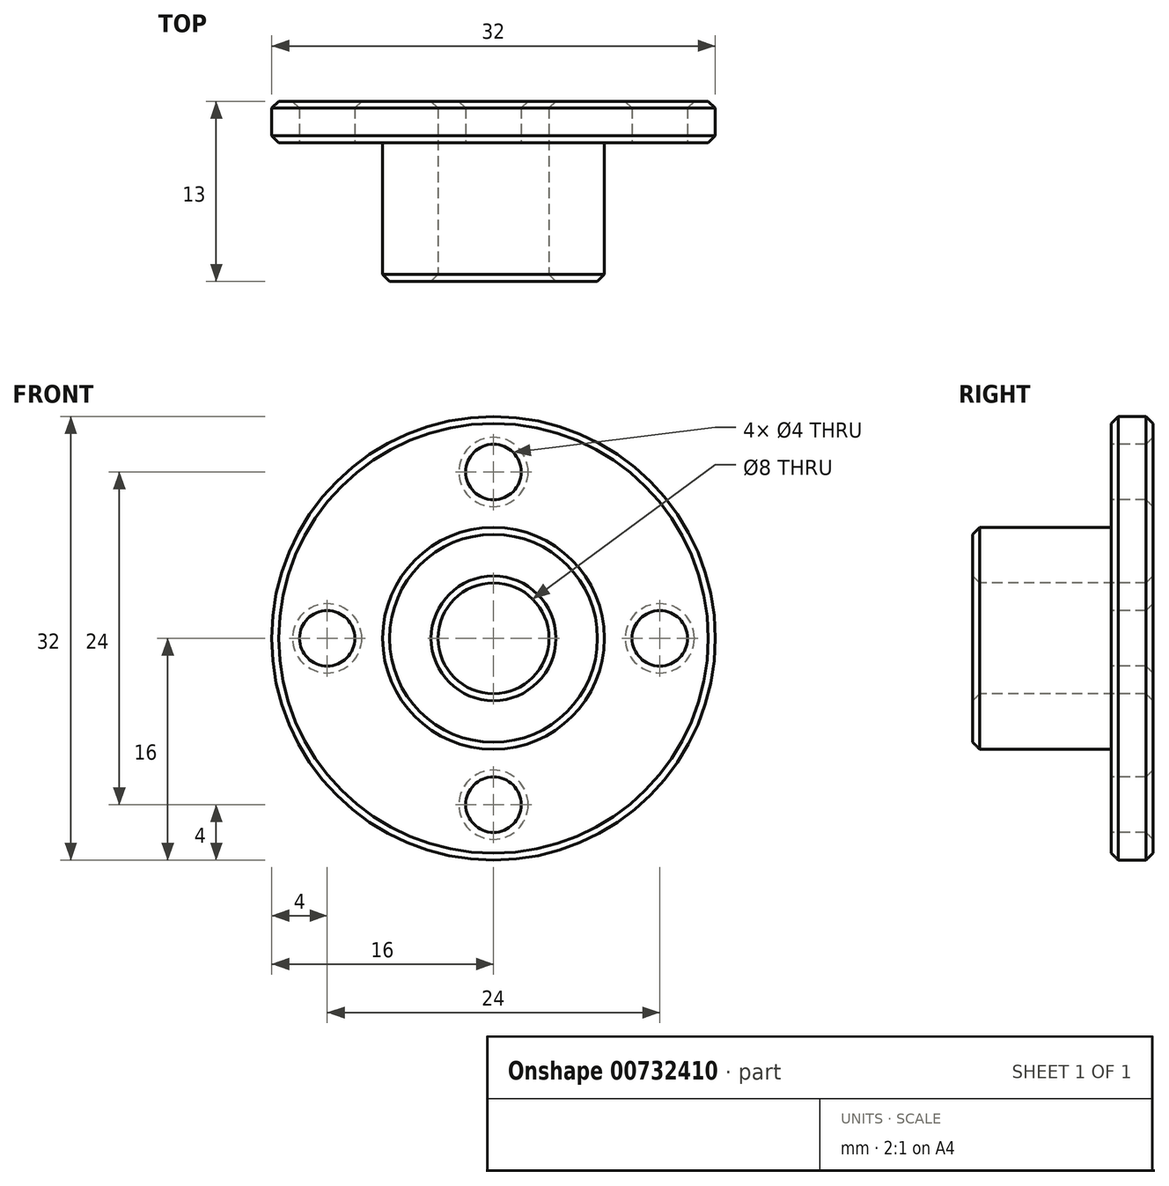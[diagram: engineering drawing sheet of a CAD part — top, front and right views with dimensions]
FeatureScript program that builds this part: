
annotation { "Feature Type Name" : "Feature", "Feature Type Description" : "" }
export const myFeature = defineFeature(function(context is Context, id is Id, definition is map)
    precondition{}
    {
        {
            var Q0;
            Q0=qCreatedBy(makeId("Front.planeOp"),FACE);
            var sketch = newSketch(context, id + "F0", { "sketchPlane" : qUnion([Q0])});
            skCircle(sketch, "E0", {"center": v(0, 0) * mm, "radius": 16 * mm});
            skSolve(sketch);
        }
        {
            var Q0;
            Q0 = qSketchRegion(id + "F0", true);
            extrude(context, id + "F1", {"entities" : qUnion([Q0]), "depth" : 3 * mm, "offsetDistance" : 25 * mm});
        }
        {
            var Q0;
            Q0=makeQuery(id+"F1.opExtrude","CAP_FACE",FACE,{"disambiguationData":[OSD([sQuery(id+"F0.wireOp",EDGE,"E0")])],"isStart":false});
            var sketch = newSketch(context, id + "F2", { "sketchPlane" : qUnion([Q0])});
            skCircle(sketch, "E1", {"center": v(0, 0) * mm, "radius": 8 * mm});
            skSolve(sketch);
        }
        {
            var Q0;
            Q0 = qSketchRegion(id + "F2", true);
            extrude(context, id + "F3", {"entities" : qUnion([Q0]), "operationType" : NewBodyOperationType.ADD, "depth" : 10 * mm, "offsetDistance" : 25 * mm});
        }
        {
            var Q0;
            Q0=makeQuery(id+"F3.opExtrude","CAP_FACE",FACE,{"disambiguationData":[OSD([sQuery(id+"F2.wireOp",EDGE,"E1")])],"isStart":false});
            var sketch = newSketch(context, id + "F4", { "sketchPlane" : qUnion([Q0])});
            skCircle(sketch, "E2", {"center": v(0, 0) * mm, "radius": 4 * mm});
            skSolve(sketch);
        }
        {
            var Q0;
            Q0 = qSketchRegion(id + "F4", true);
            extrude(context, id + "F5", {"entities" : qUnion([Q0]), "operationType" : NewBodyOperationType.REMOVE, "endBound" : BoundingType.THROUGH_ALL, "oppositeDirection" : true, "depth" : 25 * mm, "offsetDistance" : 25 * mm});
        }
        {
            var Q0;
            Q0=makeQuery(id+"F1.opExtrude","CAP_FACE",FACE,{"disambiguationData":[OSD([sQuery(id+"F0.wireOp",EDGE,"E0")])],"isStart":false});
            var sketch = newSketch(context, id + "F6", { "sketchPlane" : qUnion([Q0])});
            skCircle(sketch, "E3", {"center": v(0, 12) * mm, "radius": 2 * mm});
            skCircle(sketch, "E4.1.0", {"center": v(-12, 0) * mm, "radius": 2 * mm});
            skCircle(sketch, "E4.2.0", {"center": v(0, -12) * mm, "radius": 2 * mm});
            skCircle(sketch, "E4.3.0", {"center": v(12, 0) * mm, "radius": 2 * mm});
            skPoint(sketch, "E4.center", {"position": v(0, 0) * mm});
            skSolve(sketch);
        }
        {
            var Q0;
            Q0 = qSketchRegion(id + "F6", true);
            extrude(context, id + "F7", {"entities" : qUnion([Q0]), "operationType" : NewBodyOperationType.REMOVE, "endBound" : BoundingType.THROUGH_ALL, "oppositeDirection" : true, "depth" : 25 * mm, "offsetDistance" : 25 * mm});
        }
        {
            var Q0;
            Q0=makeQuery(id+"F3.opExtrude","CAP_FACE",FACE,{"disambiguationData":[OSD([sQuery(id+"F2.wireOp",EDGE,"E1")])],"isStart":false});
            var Q1;
            Q1=makeQuery(id+"F1.opExtrude","CAP_FACE",FACE,{"disambiguationData":[OSD([sQuery(id+"F0.wireOp",EDGE,"E0")])],"isStart":true});
            var Q2;
            Q2=makeQuery(id+"F1.opExtrude","CAP_EDGE",EDGE,{"disambiguationData":[OSD([sQuery(id+"F0.wireOp",EDGE,"E0")])],"isStart":false});
            var Q3;
            Q3=makeQuery(id+"F7.boolean.opBoolean","COPY",EDGE,{"derivedFrom":makeQuery(id+"F7.opExtrude","CAP_EDGE",EDGE,{"disambiguationData":[OSD([sQuery(id+"F6.wireOp",EDGE,"E3")])],"isStart":true})});
            var Q4;
            Q4=makeQuery(id+"F7.boolean.opBoolean","COPY",EDGE,{"derivedFrom":makeQuery(id+"F7.opExtrude","CAP_EDGE",EDGE,{"disambiguationData":[OSD([sQuery(id+"F6.wireOp",EDGE,"E4.1.0")])],"isStart":true})});
            var Q5;
            Q5=makeQuery(id+"F7.boolean.opBoolean","COPY",EDGE,{"derivedFrom":makeQuery(id+"F7.opExtrude","CAP_EDGE",EDGE,{"disambiguationData":[OSD([sQuery(id+"F6.wireOp",EDGE,"E4.3.0")])],"isStart":true})});
            var Q6;
            Q6=makeQuery(id+"F7.boolean.opBoolean","COPY",EDGE,{"derivedFrom":makeQuery(id+"F7.opExtrude","CAP_EDGE",EDGE,{"disambiguationData":[OSD([sQuery(id+"F6.wireOp",EDGE,"E4.2.0")])],"isStart":true})});
            chamfer(context, id + "F8", {"entities" : qUnion([Q0, Q1, Q2, Q3, Q4, Q5, Q6]), "width" : 0.5 * mm, "tangentPropagation" : true});
        }
    });
